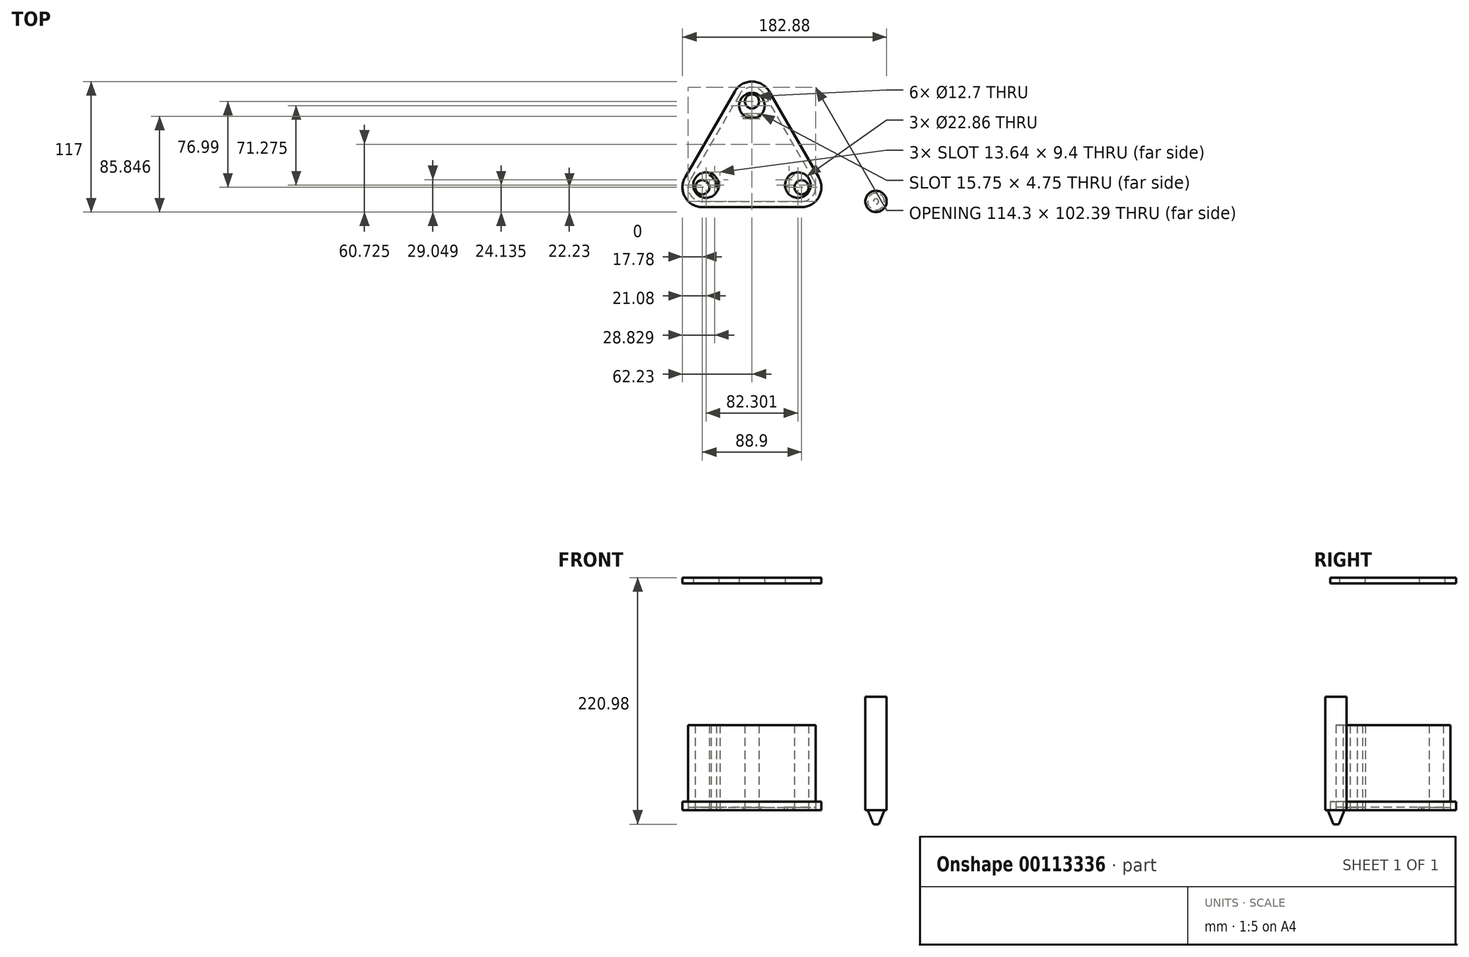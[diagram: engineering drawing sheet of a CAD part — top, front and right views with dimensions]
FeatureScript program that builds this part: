
annotation { "Feature Type Name" : "Feature", "Feature Type Description" : "" }
export const myFeature = defineFeature(function(context is Context, id is Id, definition is map)
    precondition{}
    {
        {
            var Q0;
            Q0=qCreatedBy(makeId("Top.planeOp"),FACE);
            var sketch = newSketch(context, id + "F0", { "sketchPlane" : qUnion([Q0])});
            skLineSegment(sketch, "E0", {"start": v(0, 88.29) * mm, "end": v(0, 0) * mm, "construction": true});
            skLineSegment(sketch, "E1", {"start": v(-11, 96.04) * mm, "end": v(-55.45, 19.05) * mm});
            skLineSegment(sketch, "E2.MirrorCS", {"start": v(11, 96.04) * mm, "end": v(55.45, 19.05) * mm});
            skLineSegment(sketch, "E3", {"start": v(-44.45, 0) * mm, "end": v(44.45, 0) * mm});
            skLineSegment(sketch, "E4", {"start": v(-66.45, 0) * mm, "end": v(33.22, 57.54) * mm, "construction": true});
            skLineSegment(sketch, "E5", {"start": v(66.45, 0) * mm, "end": v(-33.22, 57.54) * mm, "construction": true});
            skCircle(sketch, "E6", {"center": v(0, 89.69) * mm, "radius": 6.35 * mm});
            skCircle(sketch, "E7", {"center": v(-44.45, 12.7) * mm, "radius": 6.35 * mm});
            skCircle(sketch, "E8", {"center": v(44.45, 12.7) * mm, "radius": 6.35 * mm});
            skLineSegment(sketch, "E9", {"start": v(-44.45, 12.7) * mm, "end": v(0, 38.36) * mm, "construction": true});
            skLineSegment(sketch, "E10", {"start": v(0, 38.36) * mm, "end": v(0, 89.69) * mm, "construction": true});
            skLineSegment(sketch, "E11", {"start": v(0, 38.36) * mm, "end": v(44.45, 12.7) * mm, "construction": true});
            skPoint(sketch, "E12.visualSharp", {"position": v(66.45, 0) * mm});
            skArc(sketch, "E12.filletArc", {"start": v(44.45, 0) * mm, "mid": v(55.45, 6.35) * mm, "end": v(55.45, 19.05) * mm});
            skPoint(sketch, "E13.visualSharp", {"position": v(-66.45, 0) * mm});
            skArc(sketch, "E13.filletArc", {"start": v(-55.45, 19.05) * mm, "mid": v(-55.45, 6.35) * mm, "end": v(-44.45, 0) * mm});
            skPoint(sketch, "E14.visualSharp", {"position": v(0, 115.09) * mm});
            skArc(sketch, "E14.filletArc", {"start": v(11, 96.04) * mm, "mid": v(0, 102.39) * mm, "end": v(-11, 96.04) * mm});
            skArc(sketch, "E15.0", {"start": v(15.4, 98.58) * mm, "mid": v(0, 107.47) * mm, "end": v(-15.4, 98.58) * mm});
            skArc(sketch, "E15.1", {"start": v(-59.85, 21.6) * mm, "mid": v(-59.85, 3.8) * mm, "end": v(-44.45, -5.08) * mm});
            skLineSegment(sketch, "E15.2", {"start": v(-44.45, -5.08) * mm, "end": v(44.45, -5.08) * mm});
            skLineSegment(sketch, "E15.3", {"start": v(-15.4, 98.58) * mm, "end": v(-59.85, 21.59) * mm});
            skArc(sketch, "E15.4", {"start": v(44.45, -5.08) * mm, "mid": v(59.85, 3.81) * mm, "end": v(59.85, 21.6) * mm});
            skLineSegment(sketch, "E15.5", {"start": v(15.4, 98.58) * mm, "end": v(59.85, 21.6) * mm});
            skArc(sketch, "E16", {"start": v(-38.1, 23.7) * mm, "mid": v(-33.45, 19.05) * mm, "end": v(-31.75, 12.7) * mm});
            skLineSegment(sketch, "E17", {"start": v(-44.45, 12.7) * mm, "end": v(-27.86, 12.7) * mm, "construction": true});
            skLineSegment(sketch, "E18", {"start": v(-44.45, 12.7) * mm, "end": v(-35.96, 27.4) * mm, "construction": true});
            skArc(sketch, "E19", {"start": v(-28.7, 12.7) * mm, "mid": v(-30.81, 20.57) * mm, "end": v(-36.58, 26.34) * mm});
            skLineSegment(sketch, "E20", {"start": v(-38.1, 23.7) * mm, "end": v(-36.58, 26.34) * mm});
            skLineSegment(sketch, "E21", {"start": v(-31.75, 12.7) * mm, "end": v(-28.7, 12.7) * mm});
            skLineSegment(sketch, "E22.MirrorCS", {"start": v(38.1, 23.7) * mm, "end": v(36.58, 26.34) * mm});
            skLineSegment(sketch, "E23.MirrorCS", {"start": v(31.75, 12.7) * mm, "end": v(28.7, 12.7) * mm});
            skArc(sketch, "E24.MirrorCS", {"start": v(28.7, 12.7) * mm, "mid": v(30.81, 20.57) * mm, "end": v(36.58, 26.34) * mm});
            skArc(sketch, "E25.MirrorCS", {"start": v(38.1, 23.7) * mm, "mid": v(33.45, 19.05) * mm, "end": v(31.75, 12.7) * mm});
            skLineSegment(sketch, "E26.MirrorCS", {"start": v(-6.35, 78.7) * mm, "end": v(-7.87, 76.05) * mm});
            skLineSegment(sketch, "E27.MirrorCS", {"start": v(6.35, 78.7) * mm, "end": v(7.87, 76.05) * mm});
            skArc(sketch, "E28.MirrorCS", {"start": v(-6.35, 78.7) * mm, "mid": v(0, 76.99) * mm, "end": v(6.35, 78.7) * mm});
            skArc(sketch, "E29.MirrorCS", {"start": v(7.87, 76.05) * mm, "mid": v(0, 73.94) * mm, "end": v(-7.87, 76.05) * mm});
            skSolve(sketch);
        }
        {
            var Q0;
            Q0=makeQuery(id+"F0.imprint","IMPRINT",FACE,{"disambiguationData":[TD([[makeQuery(id+"F0.imprint","IMPRINT",EDGE,{"derivedFrom":sQuery(id+"F0.wireOp",EDGE,"E1")}),-1.0]])]});
            extrude(context, id + "F1", {"entities" : qUnion([Q0]), "depth" : 7.62 * mm});
        }
        {
            var Q0;
            Q0=makeQuery(id+"F0.imprint","IMPRINT",FACE,{"disambiguationData":[TD([[makeQuery(id+"F0.imprint","IMPRINT",EDGE,{"derivedFrom":sQuery(id+"F0.wireOp",EDGE,"E26.MirrorCS")}),1.0]])]});
            var Q1;
            Q1=makeQuery(id+"F0.imprint","IMPRINT",FACE,{"disambiguationData":[TD([[makeQuery(id+"F0.imprint","IMPRINT",EDGE,{"derivedFrom":sQuery(id+"F0.wireOp",EDGE,"E16")}),1.0]])]});
            var Q2;
            Q2=makeQuery(id+"F0.imprint","IMPRINT",FACE,{"disambiguationData":[TD([[makeQuery(id+"F0.imprint","IMPRINT",EDGE,{"derivedFrom":sQuery(id+"F0.wireOp",EDGE,"E22.MirrorCS")}),1.0]])]});
            extrude(context, id + "F2", {"entities" : qUnion([Q0, Q1, Q2]), "depth" : 76.2 * mm});
        }
        {
            var Q0;
            Q0=makeQuery(id+"F0.imprint","IMPRINT",FACE,{"disambiguationData":[TD([[makeQuery(id+"F0.imprint","IMPRINT",EDGE,{"derivedFrom":sQuery(id+"F0.wireOp",EDGE,"E1")}),1.0]])]});
            extrude(context, id + "F3", {"entities" : qUnion([Q0]), "depth" : 2.54 * mm});
        }
        {
            var Q0;
            Q0=qCreatedBy(makeId("Front.planeOp"),FACE);
            var sketch = newSketch(context, id + "F4", { "sketchPlane" : qUnion([Q0])});
            skLineSegment(sketch, "E30", {"start": v(101.6, 0) * mm, "end": v(101.6, 101.6) * mm});
            skLineSegment(sketch, "E31", {"start": v(101.6, 101.6) * mm, "end": v(111.12, 101.6) * mm});
            skLineSegment(sketch, "E32", {"start": v(111.13, 0) * mm, "end": v(111.13, 72.07) * mm, "construction": true});
            skLineSegment(sketch, "E33", {"start": v(101.6, 0) * mm, "end": v(103.63, 0) * mm});
            skLineSegment(sketch, "E34", {"start": v(103.63, 0) * mm, "end": v(108.76, -12.7) * mm});
            skLineSegment(sketch, "E35", {"start": v(108.76, -12.7) * mm, "end": v(111.13, -12.7) * mm});
            skPoint(sketch, "E36.orphan", {"position": v(111.13, -12.7) * mm});
            skLineSegment(sketch, "E37", {"start": v(111.13, 101.6) * mm, "end": v(111.13, -12.7) * mm});
            skSolve(sketch);
        }
        {
            var Q0;
            Q0=makeQuery(id+"F4.imprint","IMPRINT",FACE,{"disambiguationData":[TD([[makeQuery(id+"F4.imprint","IMPRINT",EDGE,{"derivedFrom":sQuery(id+"F4.wireOp",EDGE,"E30")}),-1.0]])]});
            var Q1;
            Q1=sQuery(id+"F4.wireOp",EDGE,"E32");
            revolve(context, id + "F5", {"entities" : qUnion([Q0]), "axis" : qUnion([Q1]), "revolveType" : RevolveType.FULL});
        }
        {
            var Q0;
            Q0=qCreatedBy(makeId("Top.planeOp"),FACE);
            cPlane(context, id + "F6", {"entities" : qUnion([Q0]), "cplaneType" : CPlaneType.OFFSET, "offset" : 203.2 * mm, "width" : 152.4 * mm, "height" : 152.4 * mm});
        }
        {
            var Q0;
            Q0=qCreatedBy(id+"F6.planeOp",FACE);
            var sketch = newSketch(context, id + "F7", { "sketchPlane" : qUnion([Q0])});
            skCircle(sketch, "E38.0", {"center": v(-44.45, 12.7) * mm, "radius": 6.35 * mm, "construction": true});
            skCircle(sketch, "E39.0", {"center": v(44.45, 12.7) * mm, "radius": 6.35 * mm, "construction": true});
            skCircle(sketch, "E40.0", {"center": v(0, 89.69) * mm, "radius": 6.35 * mm, "construction": true});
            skLineSegment(sketch, "E41", {"start": v(-44.45, 12.7) * mm, "end": v(0, 89.69) * mm, "construction": true});
            skLineSegment(sketch, "E42", {"start": v(0, 89.69) * mm, "end": v(44.45, 12.7) * mm, "construction": true});
            skLineSegment(sketch, "E43", {"start": v(-44.45, 12.7) * mm, "end": v(44.45, 12.7) * mm, "construction": true});
            skLineSegment(sketch, "E44", {"start": v(-44.45, 12.7) * mm, "end": v(22.22, 51.2) * mm, "construction": true});
            skLineSegment(sketch, "E45", {"start": v(0, 89.69) * mm, "end": v(0, 12.7) * mm, "construction": true});
            skLineSegment(sketch, "E46", {"start": v(44.45, 12.7) * mm, "end": v(-22.22, 51.2) * mm, "construction": true});
            skCircle(sketch, "E47", {"center": v(-41.15, 14.6) * mm, "radius": 11.43 * mm});
            skCircle(sketch, "E48.MirrorC", {"center": v(41.15, 14.6) * mm, "radius": 11.43 * mm});
            skCircle(sketch, "E49.MirrorC", {"center": v(0, 85.88) * mm, "radius": 11.43 * mm});
            skLineSegment(sketch, "E50.0", {"start": v(-15.4, 98.58) * mm, "end": v(-59.85, 21.59) * mm});
            skArc(sketch, "E51.0", {"start": v(15.4, 98.58) * mm, "mid": v(0, 107.47) * mm, "end": v(-15.4, 98.58) * mm});
            skLineSegment(sketch, "E52.0", {"start": v(15.4, 98.58) * mm, "end": v(59.85, 21.6) * mm});
            skArc(sketch, "E53.0", {"start": v(44.45, -5.08) * mm, "mid": v(59.85, 3.81) * mm, "end": v(59.85, 21.6) * mm});
            skLineSegment(sketch, "E54.0", {"start": v(-44.45, -5.08) * mm, "end": v(44.45, -5.08) * mm});
            skArc(sketch, "E55.0", {"start": v(-59.85, 21.59) * mm, "mid": v(-59.85, 3.8) * mm, "end": v(-44.45, -5.08) * mm});
            skSolve(sketch);
        }
        {
            var Q0;
            Q0=makeQuery(id+"F7.imprint","IMPRINT",FACE,{"disambiguationData":[TD([[makeQuery(id+"F7.imprint","IMPRINT",EDGE,{"derivedFrom":sQuery(id+"F7.wireOp",EDGE,"E47")}),-1.0]])]});
            extrude(context, id + "F8", {"entities" : qUnion([Q0]), "depth" : 5.08 * mm});
        }
    });
